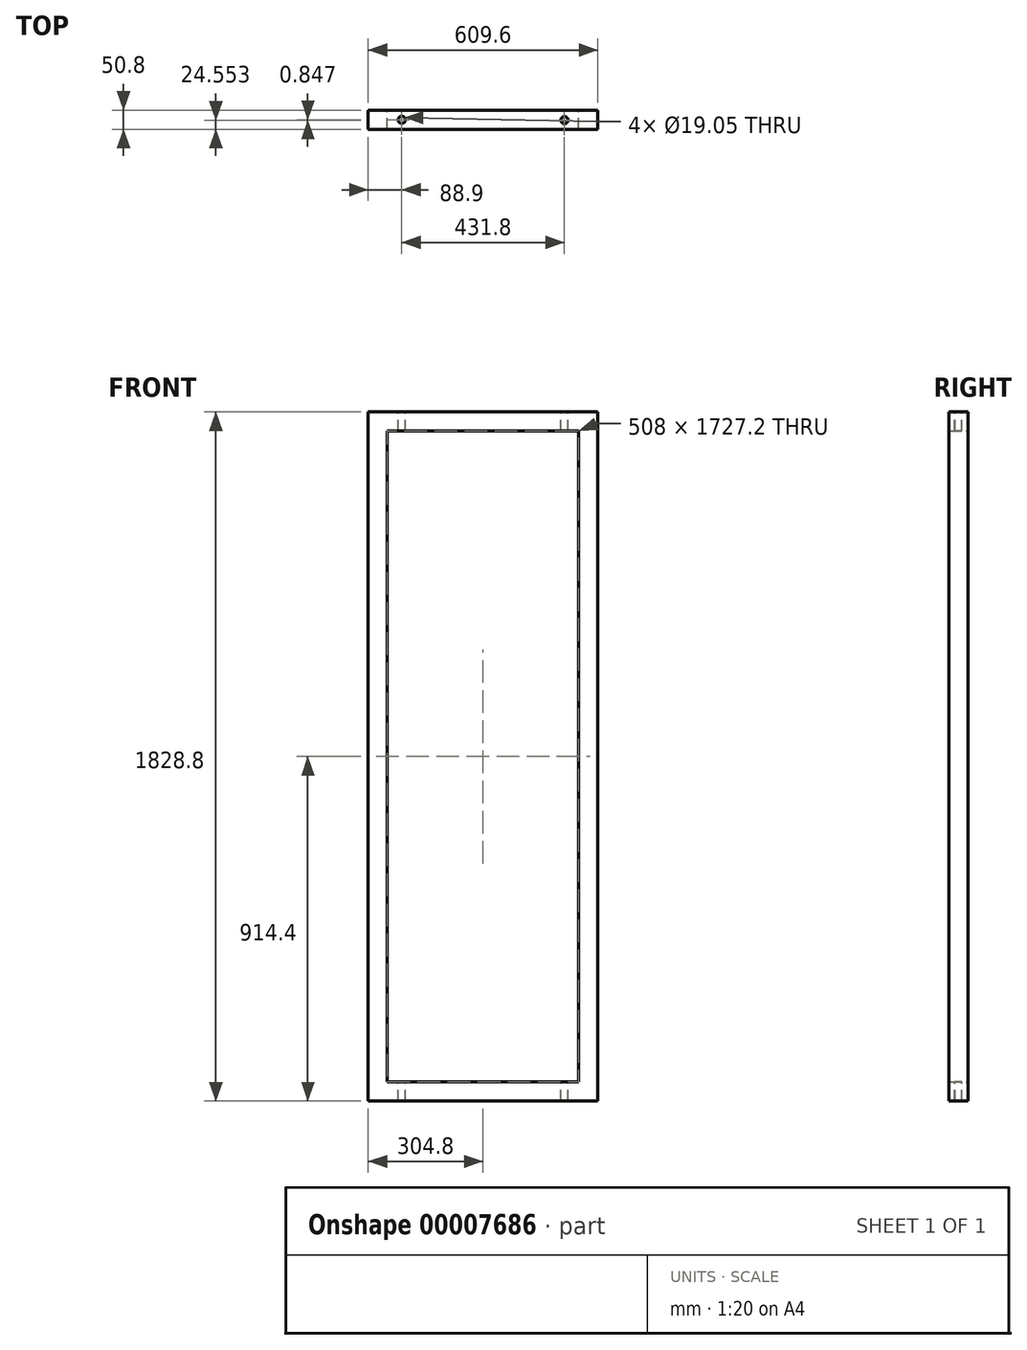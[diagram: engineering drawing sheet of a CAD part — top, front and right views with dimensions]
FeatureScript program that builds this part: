
annotation { "Feature Type Name" : "Feature", "Feature Type Description" : "" }
export const myFeature = defineFeature(function(context is Context, id is Id, definition is map)
    precondition{}
    {
        {
            var Q0;
            Q0=qCreatedBy(makeId("Front.planeOp"),FACE);
            var sketch = newSketch(context, id + "F0", { "sketchPlane" : qUnion([Q0])});
            skLineSegment(sketch, "E0.bottom", {"start": v(0, 0) * mm, "end": v(609.6, 0) * mm});
            skLineSegment(sketch, "E0.top", {"start": v(0, 1828.8) * mm, "end": v(609.6, 1828.8) * mm});
            skLineSegment(sketch, "E0.left", {"start": v(0, 0) * mm, "end": v(0, 1828.8) * mm});
            skLineSegment(sketch, "E0.right", {"start": v(609.6, 0) * mm, "end": v(609.6, 1828.8) * mm});
            skLineSegment(sketch, "E1.bottom", {"start": v(50.8, 1778) * mm, "end": v(558.8, 1778) * mm});
            skLineSegment(sketch, "E1.top", {"start": v(50.8, 50.8) * mm, "end": v(558.8, 50.8) * mm});
            skLineSegment(sketch, "E1.left", {"start": v(50.8, 1778) * mm, "end": v(50.8, 50.8) * mm});
            skLineSegment(sketch, "E1.right", {"start": v(558.8, 1778) * mm, "end": v(558.8, 50.8) * mm});
            skSolve(sketch);
        }
        {
            var Q0;
            Q0 = qSketchRegion(id + "F0", true);
            extrude(context, id + "F1", {"entities" : qUnion([Q0]), "depth" : 50.8 * mm});
        }
        {
            var Q0;
            Q0=makeQuery(id+"F1.opExtrude","SWEPT_FACE",FACE,{"disambiguationData":[OSD([sQuery(id+"F0.wireOp",EDGE,"E0.top")])]});
            var sketch = newSketch(context, id + "F2", { "sketchPlane" : qUnion([Q0])});
            skCircle(sketch, "E2", {"center": v(88.9, -25.4) * mm, "radius": 9.53 * mm});
            skCircle(sketch, "E3", {"center": v(520.7, -26.25) * mm, "radius": 9.53 * mm});
            skSolve(sketch);
        }
        {
            var Q0;
            Q0 = qSketchRegion(id + "F2", true);
            extrude(context, id + "F3", {"entities" : qUnion([Q0]), "operationType" : NewBodyOperationType.REMOVE, "oppositeDirection" : true, "depth" : 2032 * mm});
        }
    });
